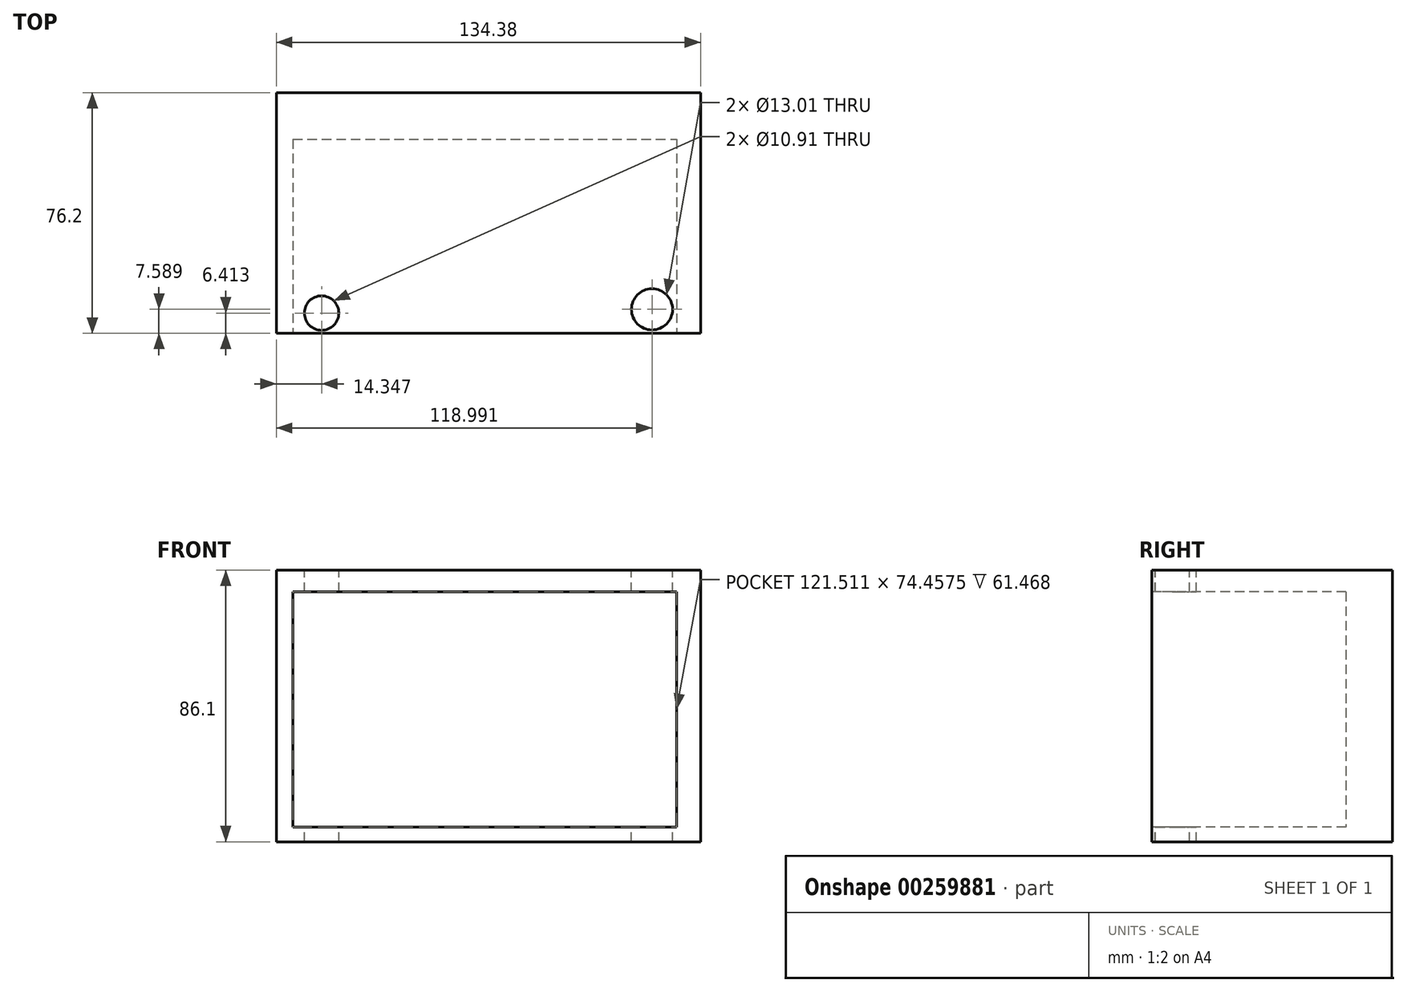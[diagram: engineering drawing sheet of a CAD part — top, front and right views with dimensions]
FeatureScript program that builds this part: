
annotation { "Feature Type Name" : "Feature", "Feature Type Description" : "" }
export const myFeature = defineFeature(function(context is Context, id is Id, definition is map)
    precondition{}
    {
        {
            var Q0;
            Q0=qCreatedBy(makeId("Front.planeOp"),FACE);
            var sketch = newSketch(context, id + "F0", { "sketchPlane" : qUnion([Q0])});
            skLineSegment(sketch, "E0.bottom", {"start": v(-66.98, 40.27) * mm, "end": v(67.4, 40.27) * mm});
            skLineSegment(sketch, "E0.top", {"start": v(-66.98, -45.83) * mm, "end": v(67.4, -45.83) * mm});
            skLineSegment(sketch, "E0.left", {"start": v(-66.98, 40.27) * mm, "end": v(-66.98, -45.83) * mm});
            skLineSegment(sketch, "E0.right", {"start": v(67.4, 40.27) * mm, "end": v(67.4, -45.83) * mm});
            skSolve(sketch);
        }
        {
            var Q0;
            Q0=makeQuery(id+"F0.imprint","IMPRINT",FACE,{"disambiguationData":[TD([[makeQuery(id+"F0.imprint","IMPRINT",EDGE,{"derivedFrom":sQuery(id+"F0.wireOp",EDGE,"E0.bottom")}),-1.0]])]});
            extrude(context, id + "F1", {"entities" : qUnion([Q0]), "oppositeDirection" : true, "depth" : 76.2 * mm});
        }
        {
            var Q0;
            Q0=makeQuery(id+"F1.opExtrude","CAP_FACE",FACE,{"disambiguationData":[OSD([sQuery(id+"F0.wireOp",EDGE,"E0.bottom"),sQuery(id+"F0.wireOp",EDGE,"E0.top"),sQuery(id+"F0.wireOp",EDGE,"E0.left"),sQuery(id+"F0.wireOp",EDGE,"E0.right")])],"isStart":true});
            var sketch = newSketch(context, id + "F2", { "sketchPlane" : qUnion([Q0])});
            skLineSegment(sketch, "E1.bottom", {"start": v(-61.74, 33.32) * mm, "end": v(59.77, 33.32) * mm});
            skLineSegment(sketch, "E1.top", {"start": v(-61.74, -41.14) * mm, "end": v(59.77, -41.14) * mm});
            skLineSegment(sketch, "E1.left", {"start": v(-61.74, 33.32) * mm, "end": v(-61.74, -41.14) * mm});
            skLineSegment(sketch, "E1.right", {"start": v(59.77, 33.32) * mm, "end": v(59.77, -41.14) * mm});
            skSolve(sketch);
        }
        {
            var Q0;
            Q0=makeQuery(id+"F2.imprint","IMPRINT",FACE,{"disambiguationData":[TD([[makeQuery(id+"F2.imprint","IMPRINT",EDGE,{"derivedFrom":sQuery(id+"F2.wireOp",EDGE,"E1.bottom")}),-1.0]])]});
            extrude(context, id + "F3", {"entities" : qUnion([Q0]), "operationType" : NewBodyOperationType.REMOVE, "oppositeDirection" : true, "depth" : 61.47 * mm});
        }
        {
            var Q0;
            Q0=makeQuery(id+"F1.opExtrude","SWEPT_FACE",FACE,{"disambiguationData":[OSD([sQuery(id+"F0.wireOp",EDGE,"E0.bottom")])]});
            var sketch = newSketch(context, id + "F4", { "sketchPlane" : qUnion([Q0])});
            skCircle(sketch, "E2", {"center": v(-52.63, 6.41) * mm, "radius": 5.45 * mm});
            skCircle(sketch, "E3", {"center": v(52.01, 7.59) * mm, "radius": 6.5 * mm});
            skSolve(sketch);
        }
        {
            var Q0;
            Q0=makeQuery(id+"F4.imprint","IMPRINT",FACE,{"disambiguationData":[TD([[makeQuery(id+"F4.imprint","IMPRINT",EDGE,{"derivedFrom":sQuery(id+"F4.wireOp",EDGE,"E2")}),1.0]])]});
            var Q1;
            Q1=makeQuery(id+"F4.imprint","IMPRINT",FACE,{"disambiguationData":[TD([[makeQuery(id+"F4.imprint","IMPRINT",EDGE,{"derivedFrom":sQuery(id+"F4.wireOp",EDGE,"E3")}),1.0]])]});
            extrude(context, id + "F5", {"entities" : qUnion([Q0, Q1]), "operationType" : NewBodyOperationType.REMOVE, "oppositeDirection" : true, "depth" : 177.8 * mm});
        }
    });
